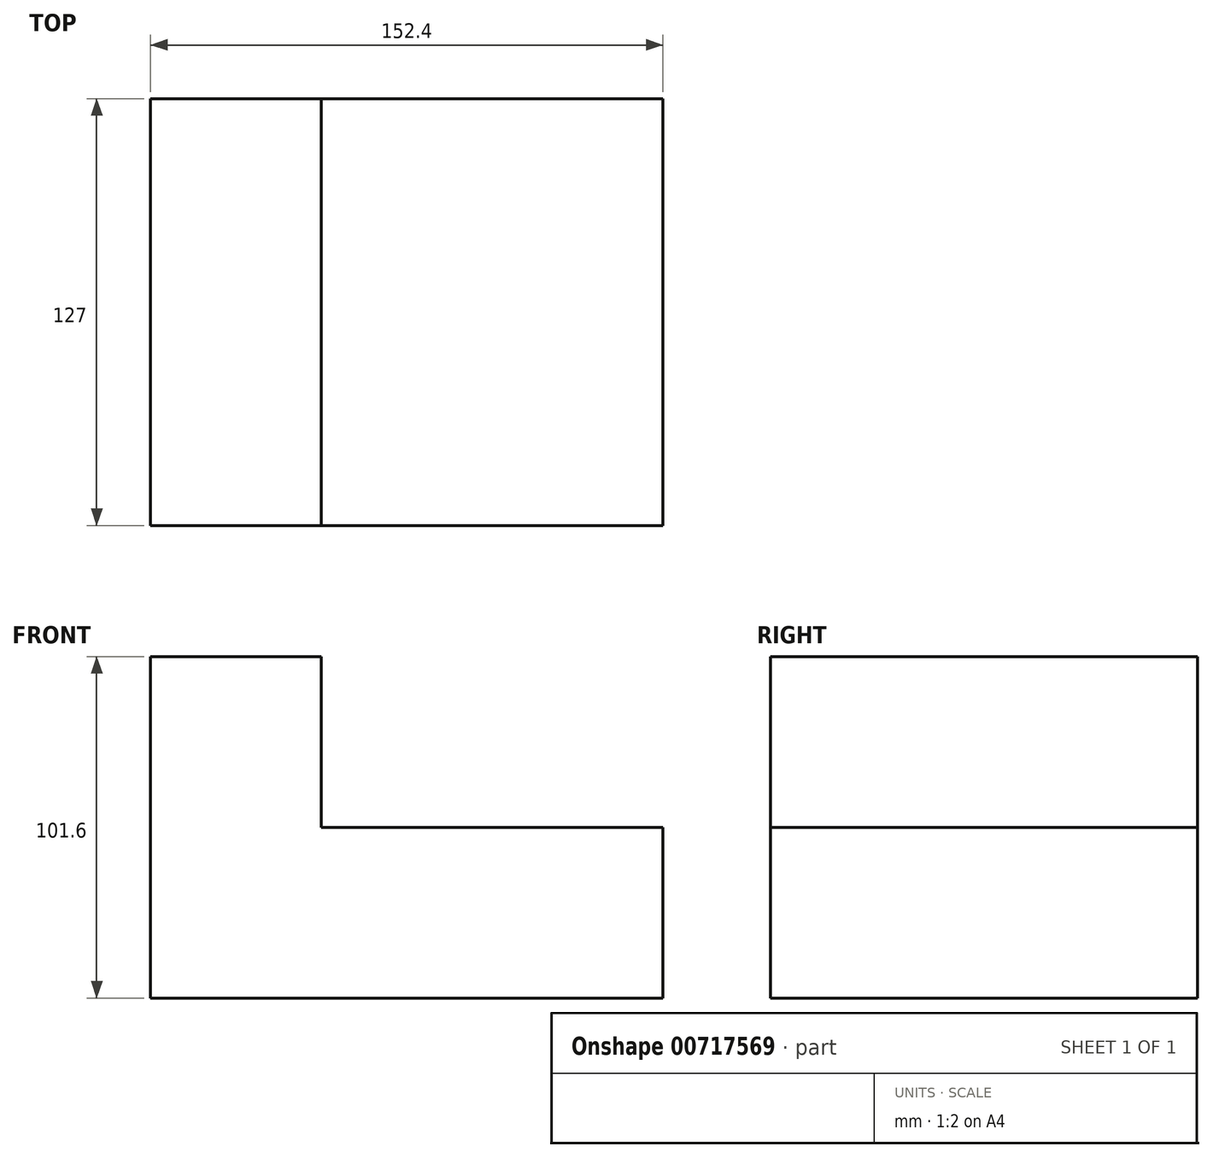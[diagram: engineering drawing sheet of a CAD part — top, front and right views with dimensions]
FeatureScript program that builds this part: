
annotation { "Feature Type Name" : "Feature", "Feature Type Description" : "" }
export const myFeature = defineFeature(function(context is Context, id is Id, definition is map)
    precondition{}
    {
        {
            var Q0;
            Q0=qCreatedBy(makeId("Front.planeOp"),FACE);
            var sketch = newSketch(context, id + "F0", { "sketchPlane" : qUnion([Q0])});
            skLineSegment(sketch, "E0", {"start": v(-96.8, -46.31) * mm, "end": v(-96.8, 55.29) * mm});
            skLineSegment(sketch, "E1", {"start": v(-96.8, -46.31) * mm, "end": v(55.6, -46.31) * mm});
            skLineSegment(sketch, "E2", {"start": v(55.6, -46.31) * mm, "end": v(55.6, 4.49) * mm});
            skLineSegment(sketch, "E3", {"start": v(55.6, 4.49) * mm, "end": v(-46, 4.49) * mm});
            skLineSegment(sketch, "E4", {"start": v(-46, 4.49) * mm, "end": v(-46, 55.29) * mm});
            skLineSegment(sketch, "E5", {"start": v(-96.8, 55.29) * mm, "end": v(-46, 55.29) * mm});
            skSolve(sketch);
        }
        {
            var Q0;
            Q0=makeQuery(id+"F0.imprint","IMPRINT",FACE,{"disambiguationData":[TD([[makeQuery(id+"F0.imprint","IMPRINT",EDGE,{"derivedFrom":sQuery(id+"F0.wireOp",EDGE,"E0")}),-1.0]])]});
            extrude(context, id + "F1", {"entities" : qUnion([Q0]), "depth" : 127 * mm, "offsetDistance" : 25.4 * mm});
        }
    });
